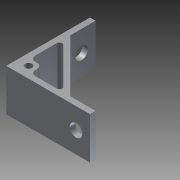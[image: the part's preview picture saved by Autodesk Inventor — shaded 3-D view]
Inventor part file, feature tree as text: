
AUTODESK INVENTOR PART (.ipt)
format: ipt  version: 2014 (Build 180170000, 170)  size: 125,952 bytes
history: native  units: mm
features: other x28, sketch x5, extrude x3, hole x2
ambient origin geometry x8: Origin, YZ Plane, XZ Plane, XY Plane, X Axis, Y Axis, Z Axis, Center Point
bodies: Solid1 (feature_tree)
feature tree (38):
  extrude  "Extrusion1"  Depth=30.0mm TaperAngle=0.0deg
  extrude  "Extrusion2"  [1 undecoded]
  extrude  "Extrusion3"  [1 undecoded]
  hole  "Drilling 2"  [1 undecoded]
  hole  "Drilling 3"  [1 undecoded]
  other  "cover_panel_hole_a_XY"
  other  "cover_panel_hole_a_YZ"
  other  "cover_panel_hole_a_ZX"
  other  "cover_panel_hole_a_X"
  other  "cover_panel_hole_a_Y"
  other  "cover_panel_hole_a_Z"
  other  "cover_panel_hole_a_Center"
  other  "cover_panel_hole_b_XY"
  other  "cover_panel_hole_b_YZ"
  other  "cover_panel_hole_b_ZX"
  other  "cover_panel_hole_b_X"
  other  "cover_panel_hole_b_Y"
  other  "cover_panel_hole_b_Z"
  other  "cover_panel_hole_b_Center"
  other  "side_1_XY"
  other  "side_1_YZ"
  other  "side_1_ZX"
  other  "side_1_X"
  other  "side_1_Y"
  other  "side_1_Z"
  other  "side_1_Center"
  other  "side_2_XY"
  other  "side_2_YZ"
  other  "side_2_ZX"
  other  "side_2_X"
  other  "side_2_Y"
  other  "side_2_Z"
  other  "side_2_Center"
  sketch  "Skizze_1"  dims[d0=30.0mm d1=0.0mm d2=32.0mm d3=0.0mm]
  sketch  "Skizze_2"  dims[d4=32.0mm d5=0.0mm]
  sketch  "Skizze_3"  dims[d6=9.0mm d7=6.0mm d8=4.0mm d9=2.0mm d10=90.0deg d11=5.0mm d12=0.0mm]
  sketch  "Sketch4"  dims[d13=9.0mm d14=6.0mm d15=4.0mm d16=2.0mm d17=90.0deg d18=5.0mm d19=0.0mm]
  sketch  "Sketch5"
note: 4 required parameter values undecoded (feature->parameter linkage not recoverable at this tier; creation-order binding heuristic only, values carry confidence <= 0.55)
